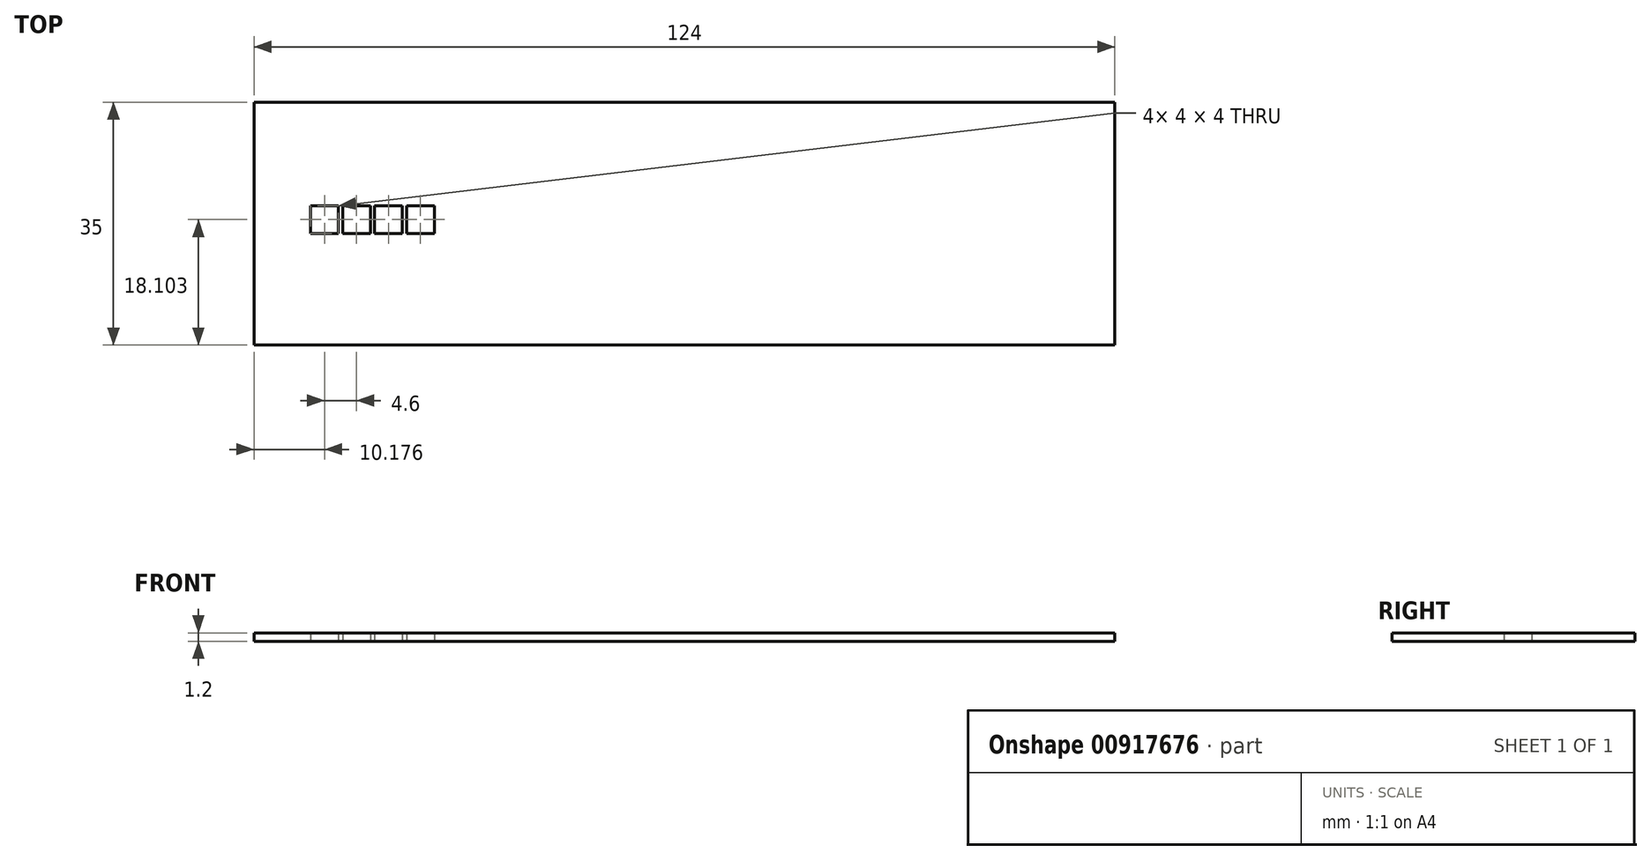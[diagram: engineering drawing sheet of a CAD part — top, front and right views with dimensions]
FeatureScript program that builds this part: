
annotation { "Feature Type Name" : "Feature", "Feature Type Description" : "" }
export const myFeature = defineFeature(function(context is Context, id is Id, definition is map)
    precondition{}
    {
        {
            var Q0;
            Q0=qCreatedBy(makeId("Top.planeOp"),FACE);
            var sketch = newSketch(context, id + "F0", { "sketchPlane" : qUnion([Q0])});
            skLineSegment(sketch, "E0.bottom", {"start": v(-124.84, 21.17) * mm, "end": v(-0.84, 21.17) * mm});
            skLineSegment(sketch, "E0.top", {"start": v(-124.84, -13.83) * mm, "end": v(-0.84, -13.83) * mm});
            skLineSegment(sketch, "E0.left", {"start": v(-124.84, 21.17) * mm, "end": v(-124.84, -13.83) * mm});
            skLineSegment(sketch, "E0.right", {"start": v(-0.84, 21.17) * mm, "end": v(-0.84, -13.83) * mm});
            skLineSegment(sketch, "E1.bottom", {"start": v(-116.66, 6.27) * mm, "end": v(-112.66, 6.27) * mm});
            skLineSegment(sketch, "E1.top", {"start": v(-116.66, 2.27) * mm, "end": v(-112.66, 2.27) * mm});
            skLineSegment(sketch, "E1.left", {"start": v(-116.66, 6.27) * mm, "end": v(-116.66, 2.27) * mm});
            skLineSegment(sketch, "E1.right", {"start": v(-112.66, 6.27) * mm, "end": v(-112.66, 2.27) * mm});
            skLineSegment(sketch, "E2.bottom", {"start": v(-112.06, 6.27) * mm, "end": v(-108.06, 6.27) * mm});
            skLineSegment(sketch, "E2.top", {"start": v(-112.06, 2.27) * mm, "end": v(-108.06, 2.27) * mm});
            skLineSegment(sketch, "E2.left", {"start": v(-112.06, 6.27) * mm, "end": v(-112.06, 2.27) * mm});
            skLineSegment(sketch, "E2.right", {"start": v(-108.06, 6.27) * mm, "end": v(-108.06, 2.27) * mm});
            skLineSegment(sketch, "E3.bottom", {"start": v(-107.46, 6.27) * mm, "end": v(-103.46, 6.27) * mm});
            skLineSegment(sketch, "E3.top", {"start": v(-107.46, 2.27) * mm, "end": v(-103.46, 2.27) * mm});
            skLineSegment(sketch, "E3.left", {"start": v(-107.46, 6.27) * mm, "end": v(-107.46, 2.27) * mm});
            skLineSegment(sketch, "E3.right", {"start": v(-103.46, 6.27) * mm, "end": v(-103.46, 2.27) * mm});
            skLineSegment(sketch, "E4.bottom", {"start": v(-102.86, 6.27) * mm, "end": v(-98.86, 6.27) * mm});
            skLineSegment(sketch, "E4.top", {"start": v(-102.86, 2.27) * mm, "end": v(-98.86, 2.27) * mm});
            skLineSegment(sketch, "E4.left", {"start": v(-102.86, 6.27) * mm, "end": v(-102.86, 2.27) * mm});
            skLineSegment(sketch, "E4.right", {"start": v(-98.86, 6.27) * mm, "end": v(-98.86, 2.27) * mm});
            skSolve(sketch);
        }
        {
            var Q0;
            Q0=makeQuery(id+"F0.imprint","IMPRINT",FACE,{"disambiguationData":[TD([[makeQuery(id+"F0.imprint","IMPRINT",EDGE,{"derivedFrom":sQuery(id+"F0.wireOp",EDGE,"E0.bottom")}),-1.0]])]});
            extrude(context, id + "F1", {"entities" : qUnion([Q0]), "depth" : 1.2 * mm, "offsetDistance" : 25 * mm});
        }
    });
